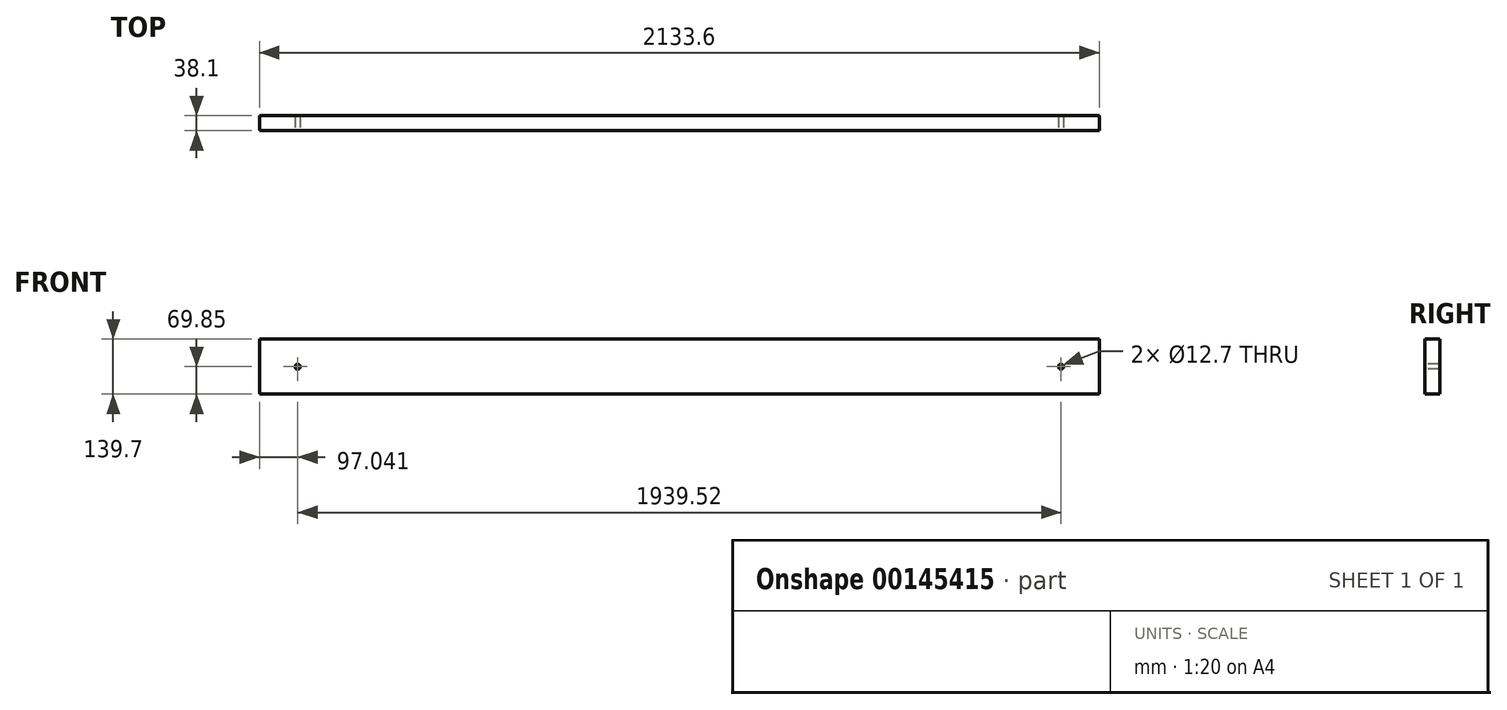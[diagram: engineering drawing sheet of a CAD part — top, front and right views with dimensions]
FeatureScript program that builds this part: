
annotation { "Feature Type Name" : "Feature", "Feature Type Description" : "" }
export const myFeature = defineFeature(function(context is Context, id is Id, definition is map)
    precondition{}
    {
        {
            var Q0;
            Q0=qCreatedBy(makeId("Front.planeOp"),FACE);
            var sketch = newSketch(context, id + "F0", { "sketchPlane" : qUnion([Q0])});
            skLineSegment(sketch, "E0.bottom", {"start": v(-1066.8, 69.85) * mm, "end": v(1066.8, 69.85) * mm});
            skLineSegment(sketch, "E0.top", {"start": v(-1066.8, -69.85) * mm, "end": v(1066.8, -69.85) * mm});
            skLineSegment(sketch, "E0.left", {"start": v(-1066.8, 69.85) * mm, "end": v(-1066.8, -69.85) * mm});
            skLineSegment(sketch, "E0.right", {"start": v(1066.8, 69.85) * mm, "end": v(1066.8, -69.85) * mm});
            skPoint(sketch, "E0.middle", {"position": v(0, 0) * mm});
            skPoint(sketch, "E1", {"position": v(-969.76, 0) * mm});
            skPoint(sketch, "E2", {"position": v(969.76, 0) * mm});
            skSolve(sketch);
        }
        {
            var Q0;
            Q0=makeQuery(id+"F0.imprint","IMPRINT",FACE,{"disambiguationData":[TD([[makeQuery(id+"F0.imprint","IMPRINT",EDGE,{"derivedFrom":sQuery(id+"F0.wireOp",EDGE,"E0.bottom")}),-1.0]])]});
            extrude(context, id + "F1", {"entities" : qUnion([Q0]), "oppositeDirection" : true, "depth" : 38.1 * mm});
        }
        {
            var Q0;
            Q0=sQuery(id+"F0.wireOp",VERTEX,"E1");
            var Q1;
            Q1=makeQuery(id+"F1.opExtrude","SWEPT_BODY",BODY,{"disambiguationData":[OSD([sQuery(id+"F0.wireOp",EDGE,"E0.bottom"),sQuery(id+"F0.wireOp",EDGE,"E0.top"),sQuery(id+"F0.wireOp",EDGE,"E0.left"),sQuery(id+"F0.wireOp",EDGE,"E0.right")])]});
            hole(context, id + "F2", {"style" : HoleStyle.SIMPLE, "endStyle" : HoleEndStyle.BLIND, "holeDiameter" : 12.7 * mm, "holeDepth" : 609.6 * mm, "startFromSketch" : true, "locations" : qUnion([Q0]), "scope" : qUnion([Q1])});
        }
        {
            var Q0;
            Q0=sQuery(id+"F0.wireOp",VERTEX,"E2");
            var Q1;
            Q1=makeQuery(id+"F1.opExtrude","SWEPT_BODY",BODY,{"disambiguationData":[OSD([sQuery(id+"F0.wireOp",EDGE,"E0.bottom"),sQuery(id+"F0.wireOp",EDGE,"E0.top"),sQuery(id+"F0.wireOp",EDGE,"E0.left"),sQuery(id+"F0.wireOp",EDGE,"E0.right")])]});
            hole(context, id + "F3", {"style" : HoleStyle.SIMPLE, "endStyle" : HoleEndStyle.BLIND, "holeDiameter" : 12.7 * mm, "holeDepth" : 609.6 * mm, "startFromSketch" : true, "locations" : qUnion([Q0]), "scope" : qUnion([Q1])});
        }
    });
